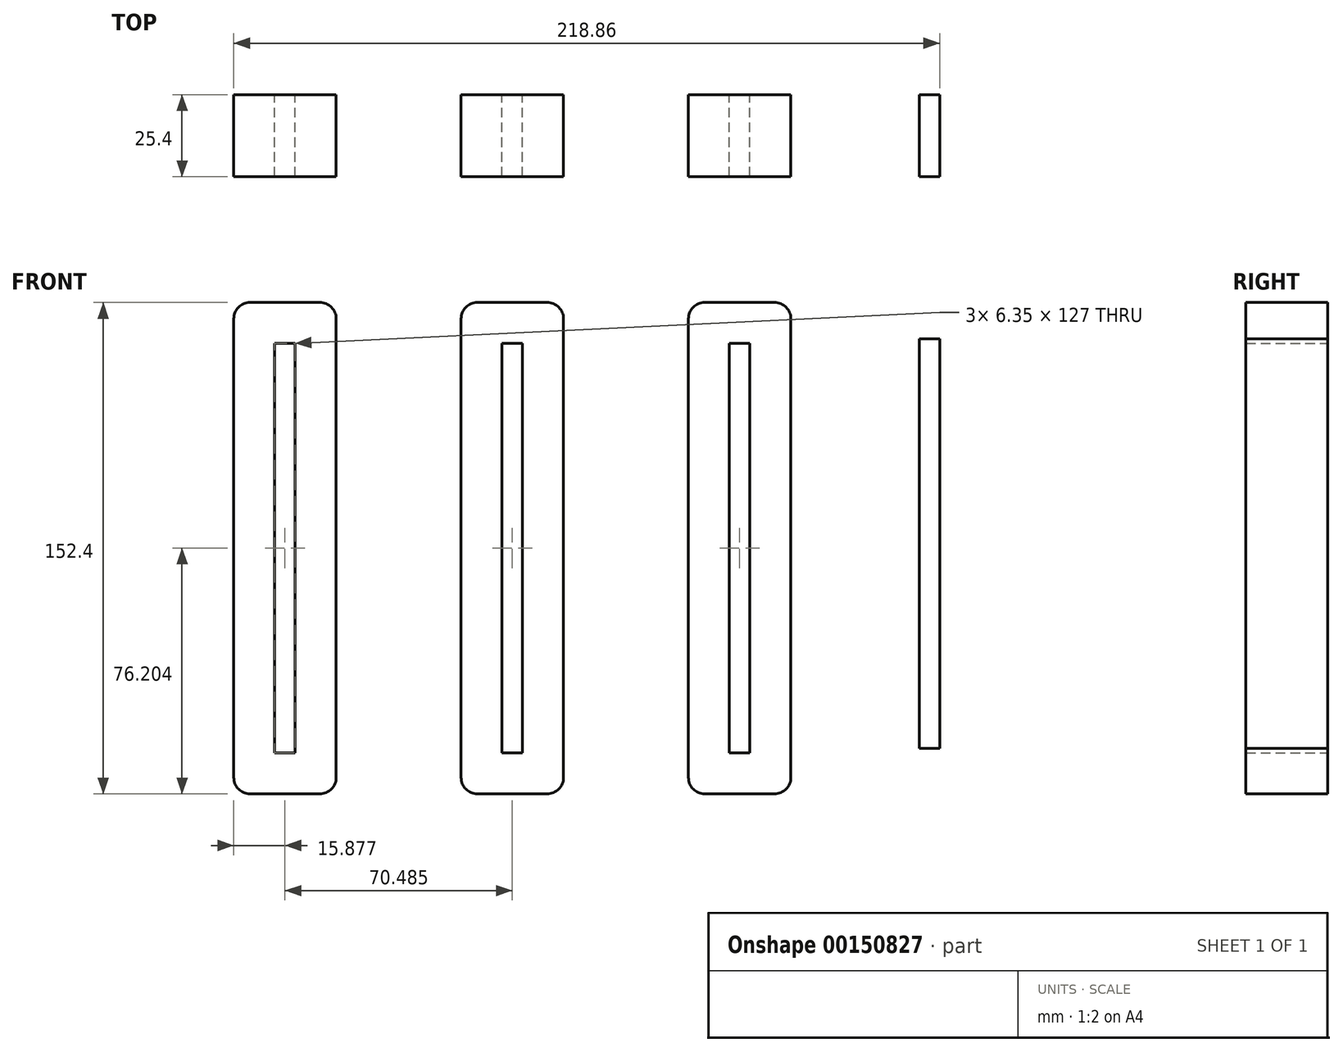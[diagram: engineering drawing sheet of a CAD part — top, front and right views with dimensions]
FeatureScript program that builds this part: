
annotation { "Feature Type Name" : "Feature", "Feature Type Description" : "" }
export const myFeature = defineFeature(function(context is Context, id is Id, definition is map)
    precondition{}
    {
        {
            var Q0;
            Q0=qCreatedBy(makeId("Front.planeOp"),FACE);
            var sketch = newSketch(context, id + "F0", { "sketchPlane" : qUnion([Q0])});
            skLineSegment(sketch, "E0.bottom", {"start": v(-45.6, 73.9) * mm, "end": v(-39.26, 73.9) * mm});
            skLineSegment(sketch, "E0.top", {"start": v(-45.6, -53.1) * mm, "end": v(-39.26, -53.1) * mm});
            skLineSegment(sketch, "E0.left", {"start": v(-45.6, 73.9) * mm, "end": v(-45.6, -53.1) * mm});
            skLineSegment(sketch, "E0.right", {"start": v(-39.26, 73.9) * mm, "end": v(-39.26, -53.1) * mm});
            skSolve(sketch);
        }
        {
            var Q0;
            Q0=qCreatedBy(makeId("Front.planeOp"),FACE);
            var sketch = newSketch(context, id + "F1", { "sketchPlane" : qUnion([Q0])});
            skLineSegment(sketch, "E1.0", {"start": v(-58.3, 86.6) * mm, "end": v(-26.56, 86.6) * mm});
            skLineSegment(sketch, "E1.1", {"start": v(-58.3, 86.6) * mm, "end": v(-58.3, -65.8) * mm});
            skLineSegment(sketch, "E1.2", {"start": v(-58.3, -65.8) * mm, "end": v(-26.56, -65.8) * mm});
            skLineSegment(sketch, "E1.3", {"start": v(-26.56, 86.6) * mm, "end": v(-26.56, -65.8) * mm});
            skSolve(sketch);
        }
        {
            var Q0;
            Q0 = qSketchRegion(id + "F1", true);
            extrude(context, id + "F2", {"entities" : qUnion([Q0]), "depth" : 25.4 * mm});
        }
        {
            var Q0;
            Q0 = qSketchRegion(id + "F0", true);
            extrude(context, id + "F3", {"entities" : qUnion([Q0]), "operationType" : NewBodyOperationType.REMOVE, "depth" : 25.4 * mm});
        }
        {
            var Q0;
            Q0=makeQuery(id+"F2.opExtrude","SWEPT_EDGE",EDGE,{"disambiguationData":[OSD([sQuery(id+"F1.wireOp",EDGE,"E1.0"),sQuery(id+"F1.wireOp",EDGE,"E1.3")])]});
            var Q1;
            Q1=makeQuery(id+"F2.opExtrude","SWEPT_EDGE",EDGE,{"disambiguationData":[OSD([sQuery(id+"F1.wireOp",EDGE,"E1.0"),sQuery(id+"F1.wireOp",EDGE,"E1.1")])]});
            var Q2;
            Q2=makeQuery(id+"F2.opExtrude","SWEPT_EDGE",EDGE,{"disambiguationData":[OSD([sQuery(id+"F1.wireOp",EDGE,"E1.1"),sQuery(id+"F1.wireOp",EDGE,"E1.2")])]});
            var Q3;
            Q3=makeQuery(id+"F2.opExtrude","SWEPT_EDGE",EDGE,{"disambiguationData":[OSD([sQuery(id+"F1.wireOp",EDGE,"E1.2"),sQuery(id+"F1.wireOp",EDGE,"E1.3")])]});
            fillet(context, id + "F4", {"entities" : qUnion([Q0, Q1, Q2, Q3]), "radius" : 5.08 * mm, "tangentPropagation" : true, "allowEdgeOverflow" : false});
        }
        {
            var Q0;
            Q0=qCreatedBy(makeId("Front.planeOp"),FACE);
            var sketch = newSketch(context, id + "F5", { "sketchPlane" : qUnion([Q0])});
            skLineSegment(sketch, "E2.bottom", {"start": v(13.23, 75.25) * mm, "end": v(19.58, 75.25) * mm});
            skLineSegment(sketch, "E2.top", {"start": v(13.23, -51.75) * mm, "end": v(19.58, -51.75) * mm});
            skLineSegment(sketch, "E2.left", {"start": v(13.23, 75.25) * mm, "end": v(13.23, -51.75) * mm});
            skLineSegment(sketch, "E2.right", {"start": v(19.58, 75.25) * mm, "end": v(19.58, -51.75) * mm});
            skSolve(sketch);
        }
        {
            var Q0;
            Q0=makeQuery(id+"F5.imprint","IMPRINT",FACE,{"disambiguationData":[TD([[makeQuery(id+"F5.imprint","IMPRINT",EDGE,{"derivedFrom":sQuery(id+"F5.wireOp",EDGE,"E2.bottom")}),-1.0]])]});
            extrude(context, id + "F6", {"entities" : qUnion([Q0]), "depth" : 25.4 * mm});
        }
        {
            var Q0;
            Q0=makeQuery(id+"F2.opExtrude","SWEPT_BODY",BODY,{"disambiguationData":[OSD([sQuery(id+"F1.wireOp",EDGE,"E1.0"),sQuery(id+"F1.wireOp",EDGE,"E1.1"),sQuery(id+"F1.wireOp",EDGE,"E1.2"),sQuery(id+"F1.wireOp",EDGE,"E1.3")])]});
            transform(context, id + "F7", {"entities" : qUnion([Q0]), "transformType" : TransformType.TRANSLATION_3D, "dx" : -70.48 * mm, "dy" : 0 * mm, "dz" : 0 * mm, "makeCopy" : true});
        }
        {
            var Q0;
            Q0=makeQuery(id+"F7.opPattern","COPY",BODY,{"derivedFrom":makeQuery(id+"F2.opExtrude","SWEPT_BODY",BODY,{"disambiguationData":[OSD([sQuery(id+"F1.wireOp",EDGE,"E1.0"),sQuery(id+"F1.wireOp",EDGE,"E1.1"),sQuery(id+"F1.wireOp",EDGE,"E1.2"),sQuery(id+"F1.wireOp",EDGE,"E1.3")])]}),"instanceName":"1"});
            transform(context, id + "F8", {"entities" : qUnion([Q0]), "transformType" : TransformType.TRANSLATION_3D, "dx" : -70.48 * mm, "dy" : 0 * mm, "dz" : 0 * mm, "makeCopy" : true});
        }
    });
